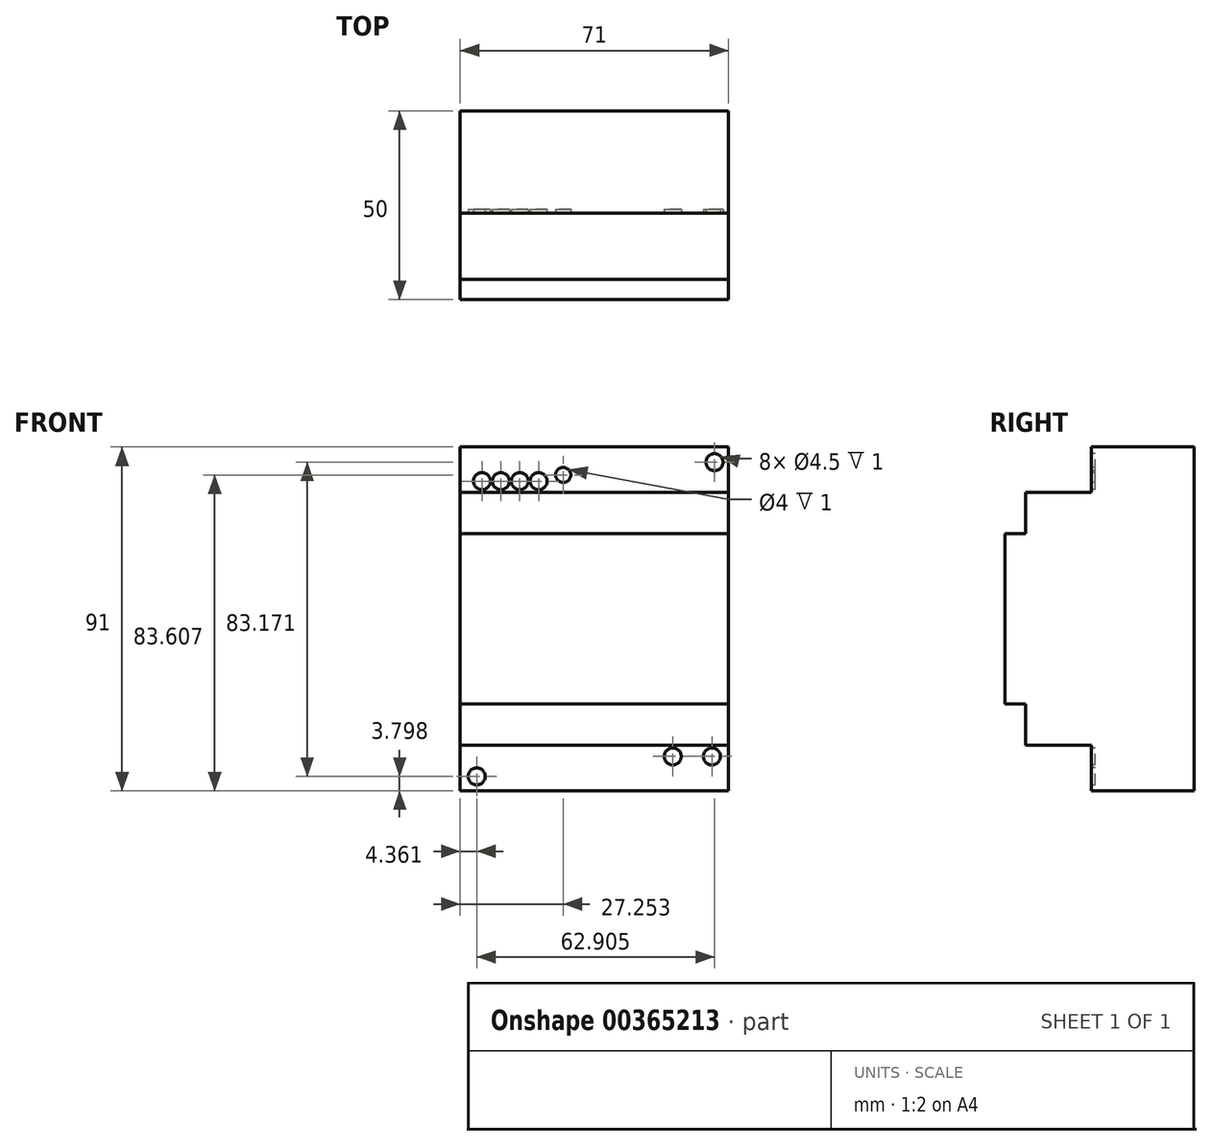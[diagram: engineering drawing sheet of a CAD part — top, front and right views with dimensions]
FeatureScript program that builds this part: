
annotation { "Feature Type Name" : "Feature", "Feature Type Description" : "" }
export const myFeature = defineFeature(function(context is Context, id is Id, definition is map)
    precondition{}
    {
        {
            var Q0;
            Q0=qCreatedBy(makeId("Front.planeOp"),FACE);
            var sketch = newSketch(context, id + "F0", { "sketchPlane" : qUnion([Q0])});
            skLineSegment(sketch, "E0.bottom", {"start": v(35.5, -45.5) * mm, "end": v(-35.5, -45.5) * mm});
            skLineSegment(sketch, "E0.top", {"start": v(35.5, 45.5) * mm, "end": v(-35.5, 45.5) * mm});
            skLineSegment(sketch, "E0.left", {"start": v(35.5, -45.5) * mm, "end": v(35.5, 45.5) * mm});
            skLineSegment(sketch, "E0.right", {"start": v(-35.5, -45.5) * mm, "end": v(-35.5, 45.5) * mm});
            skPoint(sketch, "E0.middle", {"position": v(0, 0) * mm});
            skSolve(sketch);
        }
        {
            var Q0;
            Q0 = qSketchRegion(id + "F0", true);
            extrude(context, id + "F1", {"entities" : qUnion([Q0]), "depth" : 50 * mm});
        }
        {
            var Q0;
            Q0=makeQuery(id+"F1.opExtrude","CAP_FACE",FACE,{"disambiguationData":[OSD([sQuery(id+"F0.wireOp",EDGE,"E0.bottom"),sQuery(id+"F0.wireOp",EDGE,"E0.top"),sQuery(id+"F0.wireOp",EDGE,"E0.left"),sQuery(id+"F0.wireOp",EDGE,"E0.right")])],"isStart":false});
            var sketch = newSketch(context, id + "F2", { "sketchPlane" : qUnion([Q0])});
            skLineSegment(sketch, "E1.bottom", {"start": v(-35.5, 45.5) * mm, "end": v(35.5, 45.5) * mm});
            skLineSegment(sketch, "E1.top", {"start": v(-35.5, 33.5) * mm, "end": v(35.5, 33.5) * mm});
            skLineSegment(sketch, "E1.left", {"start": v(-35.5, 45.5) * mm, "end": v(-35.5, 33.5) * mm});
            skLineSegment(sketch, "E1.right", {"start": v(35.5, 45.5) * mm, "end": v(35.5, 33.5) * mm});
            skLineSegment(sketch, "E2.bottom", {"start": v(-35.5, -45.5) * mm, "end": v(35.5, -45.5) * mm});
            skLineSegment(sketch, "E2.top", {"start": v(-35.5, -33.5) * mm, "end": v(35.5, -33.5) * mm});
            skLineSegment(sketch, "E2.left", {"start": v(-35.5, -45.5) * mm, "end": v(-35.5, -33.5) * mm});
            skLineSegment(sketch, "E2.right", {"start": v(35.5, -45.5) * mm, "end": v(35.5, -33.5) * mm});
            skSolve(sketch);
        }
        {
            var Q0;
            Q0 = qSketchRegion(id + "F2", true);
            extrude(context, id + "F3", {"entities" : qUnion([Q0]), "operationType" : NewBodyOperationType.REMOVE, "oppositeDirection" : true, "depth" : 22.9 * mm});
        }
        {
            var Q0;
            Q0=makeQuery(id+"F1.opExtrude","CAP_FACE",FACE,{"disambiguationData":[OSD([sQuery(id+"F0.wireOp",EDGE,"E0.bottom"),sQuery(id+"F0.wireOp",EDGE,"E0.top"),sQuery(id+"F0.wireOp",EDGE,"E0.left"),sQuery(id+"F0.wireOp",EDGE,"E0.right")])],"isStart":false});
            var sketch = newSketch(context, id + "F4", { "sketchPlane" : qUnion([Q0])});
            skLineSegment(sketch, "E3.bottom", {"start": v(-35.5, 33.5) * mm, "end": v(35.5, 33.5) * mm});
            skLineSegment(sketch, "E3.top", {"start": v(-35.5, 22.5) * mm, "end": v(35.5, 22.5) * mm});
            skLineSegment(sketch, "E3.left", {"start": v(-35.5, 33.5) * mm, "end": v(-35.5, 22.5) * mm});
            skLineSegment(sketch, "E3.right", {"start": v(35.5, 33.5) * mm, "end": v(35.5, 22.5) * mm});
            skLineSegment(sketch, "E4.bottom", {"start": v(-35.5, -33.5) * mm, "end": v(35.5, -33.5) * mm});
            skLineSegment(sketch, "E4.top", {"start": v(-35.5, -22.5) * mm, "end": v(35.5, -22.5) * mm});
            skLineSegment(sketch, "E4.left", {"start": v(-35.5, -33.5) * mm, "end": v(-35.5, -22.5) * mm});
            skLineSegment(sketch, "E4.right", {"start": v(35.5, -33.5) * mm, "end": v(35.5, -22.5) * mm});
            skSolve(sketch);
        }
        {
            var Q0;
            Q0 = qSketchRegion(id + "F4", true);
            extrude(context, id + "F5", {"entities" : qUnion([Q0]), "operationType" : NewBodyOperationType.REMOVE, "oppositeDirection" : true, "depth" : 5.4 * mm});
        }
        {
            var Q0;
            Q0=makeQuery(id+"F3.boolean.opBoolean","COPY",FACE,{"derivedFrom":makeQuery(id+"F3.opExtrude","CAP_FACE",FACE,{"disambiguationData":[OSD([sQuery(id+"F2.wireOp",EDGE,"E1.bottom"),sQuery(id+"F2.wireOp",EDGE,"E1.top"),sQuery(id+"F2.wireOp",EDGE,"E1.left"),sQuery(id+"F2.wireOp",EDGE,"E1.right")])],"isStart":false})});
            var sketch = newSketch(context, id + "F6", { "sketchPlane" : qUnion([Q0])});
            skCircle(sketch, "E5", {"center": v(-29.75, 36.45) * mm, "radius": 2.25 * mm});
            skCircle(sketch, "E6.1.0.0", {"center": v(-24.75, 36.45) * mm, "radius": 2.25 * mm});
            skCircle(sketch, "E6.2.0.0", {"center": v(-19.75, 36.45) * mm, "radius": 2.25 * mm});
            skCircle(sketch, "E6.3.0.0", {"center": v(-14.75, 36.45) * mm, "radius": 2.25 * mm});
            skLineSegment(sketch, "E6.direction1", {"start": v(-29.75, 36.45) * mm, "end": v(-24.75, 36.45) * mm, "construction": true});
            skCircle(sketch, "E7", {"center": v(20.72, -36.42) * mm, "radius": 2.25 * mm});
            skLineSegment(sketch, "E8", {"start": v(20.72, -36.42) * mm, "end": v(31.09, -36.42) * mm, "construction": true});
            skCircle(sketch, "E9", {"center": v(31.09, -36.42) * mm, "radius": 2.25 * mm});
            skLineSegment(sketch, "E10.bottom", {"start": v(-23.53, 17.54) * mm, "end": v(-21.03, 17.54) * mm});
            skLineSegment(sketch, "E10.top", {"start": v(-23.53, 12.04) * mm, "end": v(-21.03, 12.04) * mm});
            skLineSegment(sketch, "E10.left", {"start": v(-23.53, 17.54) * mm, "end": v(-23.53, 12.04) * mm});
            skLineSegment(sketch, "E10.right", {"start": v(-21.03, 17.54) * mm, "end": v(-21.03, 12.04) * mm});
            skLineSegment(sketch, "E11", {"start": v(-23.53, 12.04) * mm, "end": v(-23.53, 3.25) * mm, "construction": true});
            skLineSegment(sketch, "E12.bottom", {"start": v(-23.53, 11.48) * mm, "end": v(-21.03, 11.48) * mm});
            skLineSegment(sketch, "E12.top", {"start": v(-23.53, 5.98) * mm, "end": v(-21.03, 5.98) * mm});
            skLineSegment(sketch, "E12.left", {"start": v(-23.53, 11.48) * mm, "end": v(-23.53, 5.98) * mm});
            skLineSegment(sketch, "E12.right", {"start": v(-21.03, 11.48) * mm, "end": v(-21.03, 5.98) * mm});
            skCircle(sketch, "E13", {"center": v(31.77, 41.47) * mm, "radius": 2.25 * mm});
            skCircle(sketch, "E14", {"center": v(-31.14, -41.7) * mm, "radius": 2.25 * mm});
            skCircle(sketch, "E15", {"center": v(-8.25, 38.1) * mm, "radius": 2 * mm});
            skSolve(sketch);
        }
        {
            var Q0;
            Q0=makeQuery(id+"F6.imprint","IMPRINT",FACE,{"disambiguationData":[TD([[makeQuery(id+"F6.imprint","IMPRINT",EDGE,{"derivedFrom":sQuery(id+"F6.wireOp",EDGE,"E5")}),1.0]])]});
            var Q1;
            Q1=makeQuery(id+"F6.imprint","IMPRINT",FACE,{"disambiguationData":[TD([[makeQuery(id+"F6.imprint","IMPRINT",EDGE,{"derivedFrom":sQuery(id+"F6.wireOp",EDGE,"E6.1.0.0")}),1.0]])]});
            var Q2;
            Q2=makeQuery(id+"F6.imprint","IMPRINT",FACE,{"disambiguationData":[TD([[makeQuery(id+"F6.imprint","IMPRINT",EDGE,{"derivedFrom":sQuery(id+"F6.wireOp",EDGE,"E6.2.0.0")}),1.0]])]});
            var Q3;
            Q3=makeQuery(id+"F6.imprint","IMPRINT",FACE,{"disambiguationData":[TD([[makeQuery(id+"F6.imprint","IMPRINT",EDGE,{"derivedFrom":sQuery(id+"F6.wireOp",EDGE,"E6.3.0.0")}),1.0]])]});
            var Q4;
            Q4=makeQuery(id+"F6.imprint","IMPRINT",FACE,{"disambiguationData":[TD([[makeQuery(id+"F6.imprint","IMPRINT",EDGE,{"derivedFrom":sQuery(id+"F6.wireOp",EDGE,"E15")}),1.0]])]});
            var Q5;
            Q5=makeQuery(id+"F6.imprint","IMPRINT",FACE,{"disambiguationData":[TD([[makeQuery(id+"F6.imprint","IMPRINT",EDGE,{"derivedFrom":sQuery(id+"F6.wireOp",EDGE,"E13")}),1.0]])]});
            var Q6;
            Q6=makeQuery(id+"F6.imprint","IMPRINT",FACE,{"disambiguationData":[TD([[makeQuery(id+"F6.imprint","IMPRINT",EDGE,{"derivedFrom":sQuery(id+"F6.wireOp",EDGE,"E14")}),1.0]])]});
            var Q7;
            Q7=makeQuery(id+"F6.imprint","IMPRINT",FACE,{"disambiguationData":[TD([[makeQuery(id+"F6.imprint","IMPRINT",EDGE,{"derivedFrom":sQuery(id+"F6.wireOp",EDGE,"E7")}),1.0]])]});
            var Q8;
            Q8=makeQuery(id+"F6.imprint","IMPRINT",FACE,{"disambiguationData":[TD([[makeQuery(id+"F6.imprint","IMPRINT",EDGE,{"derivedFrom":sQuery(id+"F6.wireOp",EDGE,"E9")}),1.0]])]});
            extrude(context, id + "F7", {"entities" : qUnion([Q0, Q1, Q2, Q3, Q4, Q5, Q6, Q7, Q8]), "operationType" : NewBodyOperationType.REMOVE, "oppositeDirection" : true, "depth" : 1 * mm});
        }
    });
